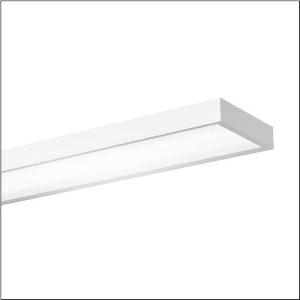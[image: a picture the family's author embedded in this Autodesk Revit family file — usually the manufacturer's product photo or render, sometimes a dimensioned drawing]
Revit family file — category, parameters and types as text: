
# Revit family: sport_31_51hs12dd4gca
name_source: partatom
category: Lighting Fixtures
units: mm (PartAtom-declared; Revit-internal decimal feet)

## family parameters
Cut with Voids When Loaded = No
Host = Face
Light Source = No
Part Type = Normal
Room Calculation Point = No
Round Connector Dimension = Use Diameter
Shared = No

## types (1)
- --- (1 x LED, 15290 lm, 113 W, 4000K)
    Apparent Load = 113 VA
    CIE Flux Codes = 65 89 97 100 100
    Color Rendering = 80
    Color Temperature = 4000K
    Default Elevation = 1800 mm
    Description = Sport 31, high bay luminaire, primary light control with reflector, of sheet steel, primary anti-glare with prismatic structure, of PC, primary optical cover: cover panel, of PC, light emission: direct distribution, primary light characteristic: symmetric, installation type: suspended mounting, recessed, surface-mounted, LED, rated luminous flux: 16.000lm, luminous efficacy: 137lm/W, light colour: 840, colour temperature: 4000K, control gear: DALI 2, with terminal, 5-pole, max. 2.5mm², mains connection: 220..240V, AC/DC, 50/60Hz, rated input power: 117W, housing, of sheet steel, traffic white (RAL 9016), length: 1.540mm, width: 415mm, height: 95mm, protection rating (complete): IP20, protection rating (lamp compartment, on room side): IP50, insulation class (complete): insulation class I (protective earthing), certification: CE, ENEC, UKCA, ball protection: ball impact resistant with ceiling mounting or chain suspension, impact resistance: IK08, permissible operating ambient temperature: -20..+35°C, standard: DIN 18032-3, EN 60598-2-22, packaging unit: 1 piece
    Height = 100 mm  [stored 0.328084 ft]
    Lamp = 1 x LED
    Lamp Light Flux = 15290 lm
    Lamp Power = 113 W
    Lamp count = 1
    Length = 1500 mm
    Luminous efficacy = 135 lm/W
    Manufacturer = Siteco
    ModVariant = No
    Model = 51HS12DD4GCA
    Mounting Place = Ceiling
    Mounting Type = Pendant
    Number of Poles = 1
    OnlyDefault = Yes
    Power Factor = 1
    Product Name = Sport 31
    Product group = high bay luminaire
    ProductGroupID = 902
    Protection Class = Protection class I
    Protection Degree = IP 20
    RLX_Detail_Level = 1
    RLX_Emergency_Light_Flux = 0 lm
    RLX_Emergency_Type = 0
    RLX_Emergency_Type_DB = No
    RlxData = <blob elided: 24085 chars, md5=c79a7acf>
    Socket = socket
    Standby Power = 0 W
    System Light Flux = 15290 lm
    System Power = 113 W
    Type Comments = factory setting: luminous flux: 100 % | dim-lin: 254 | 558 mA
    Type Image = l_1397495.jpg
    URL = http://relux.com
    VarID = @adj_198395
    Voltage = 0 V
    Weight = 0.00 kg
    Width = 415 mm

note: [stored X ft] marks values corroborated as IEEE doubles in the binary element streams (Revit-internal decimal feet)

## geometry (parser evidence)
native form markers: Blend x4, Sweep x10
no freeform markers — native parametric forms only
